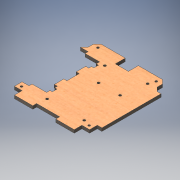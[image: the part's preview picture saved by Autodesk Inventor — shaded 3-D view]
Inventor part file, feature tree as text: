
AUTODESK INVENTOR PART (.ipt)
format: ipt  version: 2019 (Build 230136000, 136)  size: 240,128 bytes
history: native  units: mm
features: sketch x3, extrude x2, hole x2, other x1
ambient origin geometry x8: Origin, YZ Plane, XZ Plane, XY Plane, X Axis, Y Axis, Z Axis, Center Point
bodies: Body1 (feature_tree)
feature tree (8):
  other  "Твердое тело1"
  extrude  "Выдавливание1"  Depth=30.0mm
  hole  "Отверстие1"  [1 undecoded]
  extrude  "Выдавливание2"  Depth=10.0mm
  hole  "Отверстие2"  [1 undecoded]
  sketch  "Эскиз1"
  sketch  "Эскиз4"
  sketch  "Эскиз5"
note: 2 required parameter values undecoded (feature->parameter linkage not recoverable at this tier; creation-order binding heuristic only, values carry confidence <= 0.55)
